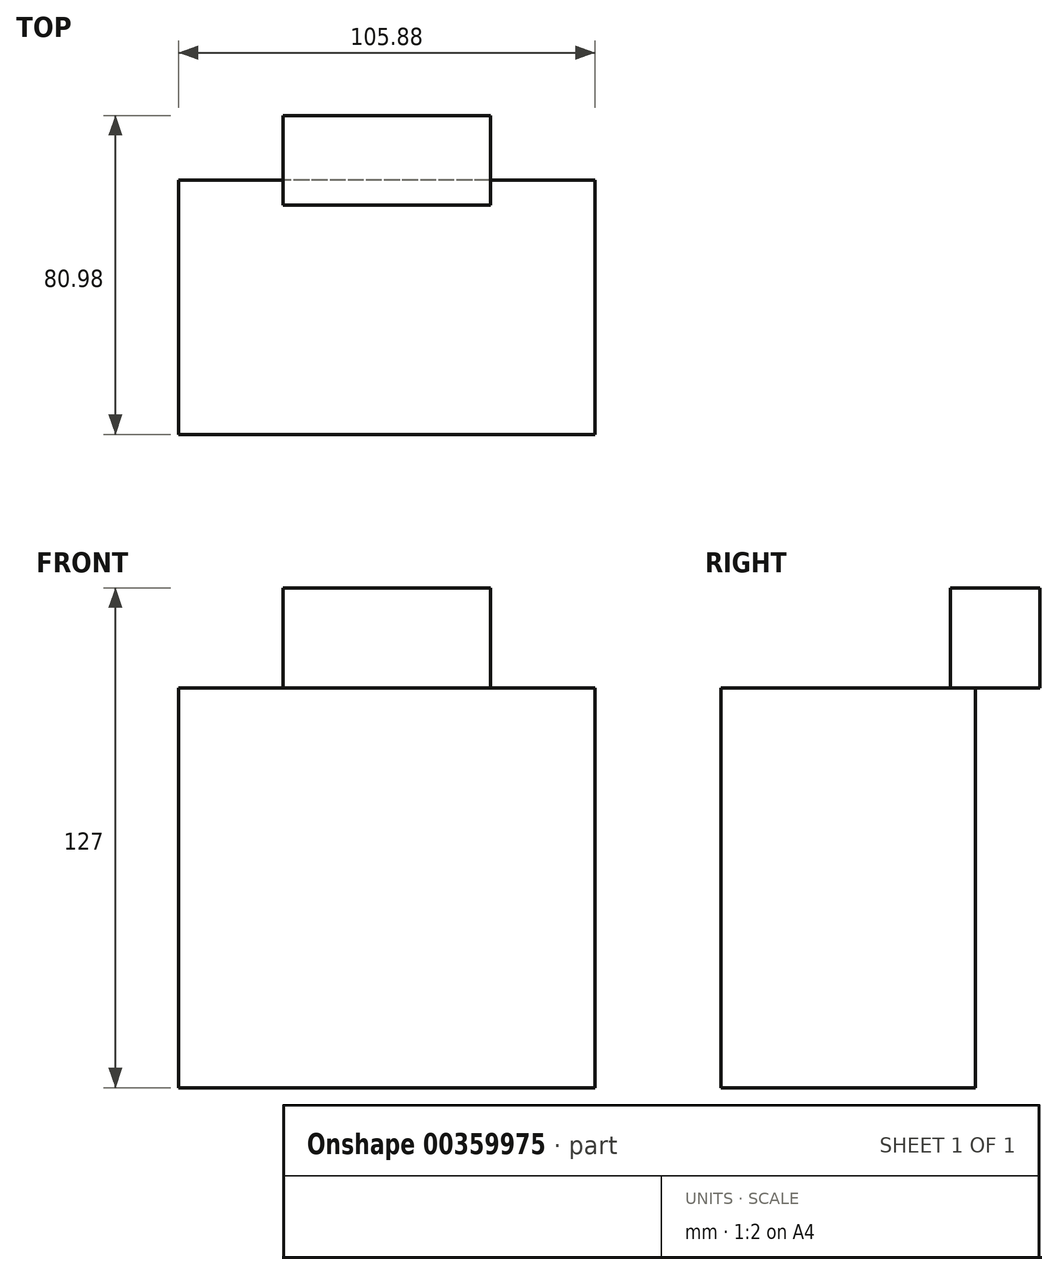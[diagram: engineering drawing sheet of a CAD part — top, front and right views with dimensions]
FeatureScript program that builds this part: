
annotation { "Feature Type Name" : "Feature", "Feature Type Description" : "" }
export const myFeature = defineFeature(function(context is Context, id is Id, definition is map)
    precondition{}
    {
        {
            var Q0;
            Q0=qCreatedBy(makeId("Top.planeOp"),FACE);
            var sketch = newSketch(context, id + "F0", { "sketchPlane" : qUnion([Q0])});
            skLineSegment(sketch, "E0.bottom", {"start": v(52.94, 32.32) * mm, "end": v(-52.94, 32.32) * mm});
            skLineSegment(sketch, "E0.top", {"start": v(52.94, -32.32) * mm, "end": v(-52.94, -32.32) * mm});
            skLineSegment(sketch, "E0.left", {"start": v(52.94, 32.32) * mm, "end": v(52.94, -32.32) * mm});
            skLineSegment(sketch, "E0.right", {"start": v(-52.94, 32.32) * mm, "end": v(-52.94, -32.32) * mm});
            skPoint(sketch, "E0.middle", {"position": v(0, 0) * mm});
            skSolve(sketch);
        }
        {
            var Q0;
            Q0 = qSketchRegion(id + "F0", true);
            extrude(context, id + "F1", {"entities" : qUnion([Q0]), "oppositeDirection" : true, "depth" : 101.6 * mm});
        }
        {
            var Q0;
            Q0=qCreatedBy(makeId("Top.planeOp"),FACE);
            var sketch = newSketch(context, id + "F2", { "sketchPlane" : qUnion([Q0])});
            skLineSegment(sketch, "E1.bottom", {"start": v(26.34, 25.95) * mm, "end": v(-26.34, 25.95) * mm});
            skLineSegment(sketch, "E1.top", {"start": v(26.34, 48.66) * mm, "end": v(-26.34, 48.66) * mm});
            skLineSegment(sketch, "E1.left", {"start": v(26.34, 25.95) * mm, "end": v(26.34, 48.66) * mm});
            skLineSegment(sketch, "E1.right", {"start": v(-26.34, 25.95) * mm, "end": v(-26.34, 48.66) * mm});
            skPoint(sketch, "E1.middle", {"position": v(0, 37.3) * mm});
            skSolve(sketch);
        }
        {
            var Q0;
            Q0 = qSketchRegion(id + "F2", true);
            extrude(context, id + "F3", {"entities" : qUnion([Q0]), "operationType" : NewBodyOperationType.ADD, "depth" : 25.4 * mm});
        }
    });
